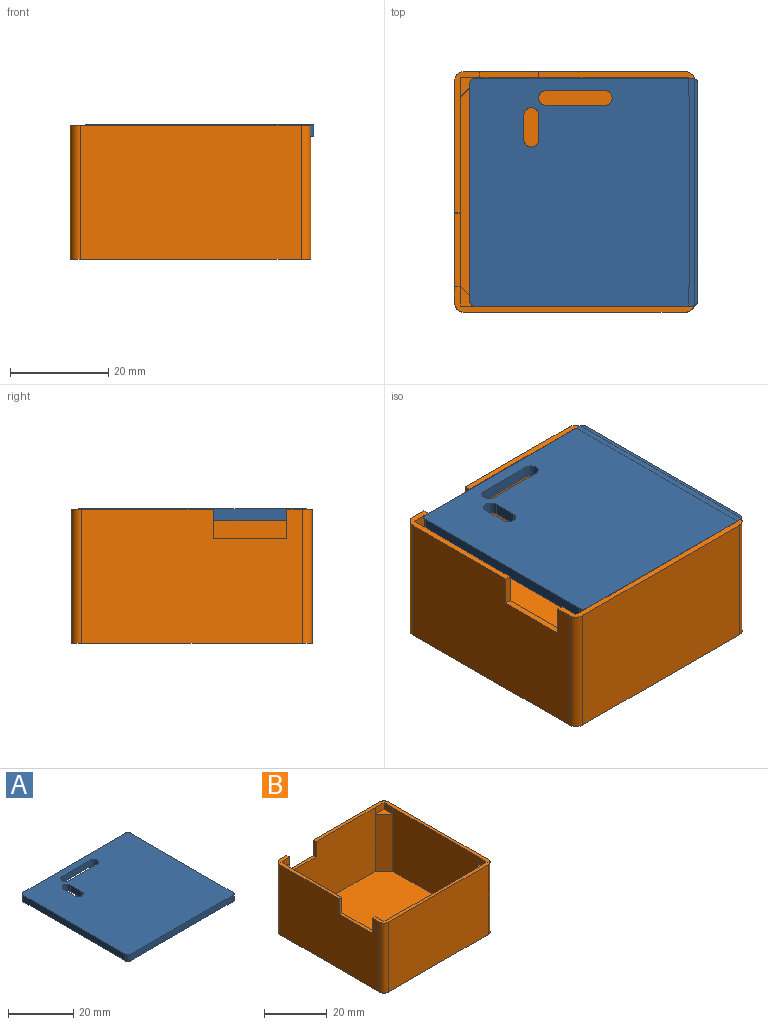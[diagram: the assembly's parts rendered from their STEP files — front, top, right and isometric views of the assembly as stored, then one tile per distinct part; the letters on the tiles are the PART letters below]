
ASSEMBLY  parts=2 mates=1
PART A: 18 faces, bbox 46.4x46.4x2.4 mm
  f0: plane 46.4x46.4mm, normal (0,0,1), area 2087mm2, adj f2,f3,f4,f5,f6,f7,f8,f9
  f1: plane 46.4x46.4mm, normal (0,0,-1), area 2087mm2, adj f2,f3,f4,f5,f6,f7,f8,f9
  f2: plane 44.4x2.4mm, normal (0,1,0), area 106.6mm2, adj f0,f1,f6,f9
  f3: plane 44.4x2.4mm, normal (-1,0,0), area 106.6mm2, adj f0,f1,f6,f7
  f4: plane 44.4x2.4mm, normal (0,-1,0), area 106.6mm2, adj f0,f1,f7,f8
  f5: plane 44.4x2.4mm, normal (1,0,0), area 106.6mm2, adj f0,f1,f8,f9
  f6: cylinder r=1mm len=2.4mm, axis (0,0,1), area 3.8mm2, adj f0,f1,f2,f3
  f7: cylinder r=1mm len=2.4mm, axis (0,0,-1), area 3.8mm2, adj f0,f1,f3,f4
  f8: cylinder r=1mm len=2.4mm, axis (0,0,1), area 3.8mm2, adj f0,f1,f4,f5
  f9: cylinder r=1mm len=2.4mm, axis (0,0,-1), area 3.8mm2, adj f0,f1,f2,f5
  f10: plane 12x2.4mm, normal (0,-1,0), area 28.8mm2, adj f0,f1,f16,f17
  f11: plane 12x2.4mm, normal (0,1,0), area 28.8mm2, adj f0,f1,f16,f17
  f12: plane 5x2.4mm, normal (1,0,0), area 12mm2, adj f0,f1,f14,f15
  f13: plane 5x2.4mm, normal (-1,0,0), area 12mm2, adj f0,f1,f14,f15
  f14: cylinder r=1.5mm len=3mm, axis (0,0,-1), area 11.3mm2, adj f0,f1,f12,f13
  f15: cylinder r=1.5mm len=3mm, axis (0,0,1), area 11.3mm2, adj f0,f1,f12,f13
  f16: cylinder r=1.5mm len=3mm, axis (0,0,-1), area 11.3mm2, adj f0,f1,f10,f11
  f17: cylinder r=1.5mm len=3mm, axis (0,0,-1), area 11.3mm2, adj f0,f1,f10,f11
PART B: 38 faces, bbox 49x49x27.3 mm
  f0: plane 28.8x5.2mm, normal (0,0,1), area 38.9mm2, adj f4,f5,f11,f14,f18,f29,f30,f32
  f1: plane 49x49mm, normal (0,0,1), area 156.3mm2, adj f2,f3,f4,f5,f6,f7,f9,f10
  f2: plane 24.9x4mm, normal (-0.71,-0.71,0), area 126.5mm2, adj f1,f9,f10,f13,f26,f27,f28
  f3: plane 24.9x4mm, normal (-0.71,0.71,0), area 126.5mm2, adj f1,f9,f12,f13,f20,f21,f22
  f4: plane 45x27.3mm, normal (0,1,0), area 1156.5mm2, adj f0,f1,f8,f14,f17,f35,f36,f37
  f5: plane 45x27.3mm, normal (-1,0,0), area 1138.5mm2, adj f0,f1,f8,f14,f15,f32,f33,f34
  f6: plane 45x27.3mm, normal (0,-1,0), area 1228.5mm2, adj f1,f8,f15,f16
  f7: plane 45x27.3mm, normal (1,0,0), area 1228.5mm2, adj f1,f8,f16,f17
  f8: plane 49x49mm, normal (0,0,-1), area 2397.6mm2, adj f4,f5,f6,f7,f14,f15,f16,f17
  f9: plane 38.6x24.9mm, normal (-1,0,0), area 961.1mm2, adj f1,f2,f3,f13
  f10: plane 38.6x24.9mm, normal (0,-1,0), area 889.1mm2, adj f1,f2,f13,f18,f35,f36
  f11: plane 38.6x24.9mm, normal (1,0,0), area 871.1mm2, adj f0,f13,f18,f19,f32,f33
  f12: plane 38.6x24.9mm, normal (0,1,0), area 961.1mm2, adj f1,f3,f13,f19
  f13: plane 46.6x46.6mm, normal (0,0,1), area 2139.6mm2, adj f2,f3,f9,f10,f11,f12,f18,f19
  f14: cylinder r=2mm len=27.3mm, axis (0,0,1), area 85.8mm2, adj f0,f4,f5,f8
  f15: cylinder r=2mm len=27.3mm, axis (0,0,-1), area 85.8mm2, adj f1,f5,f6,f8
  f16: cylinder r=2mm len=27.3mm, axis (0,0,1), area 85.8mm2, adj f1,f6,f7,f8
  f17: cylinder r=2mm len=27.3mm, axis (0,0,-1), area 85.8mm2, adj f1,f4,f7,f8
  f18: plane 24.9x4mm, normal (0.71,-0.71,0), area 126.5mm2, adj f0,f10,f11,f13,f29,f30,f31,f37
  f19: plane 24.9x4mm, normal (0.71,0.71,0), area 126.5mm2, adj f1,f11,f12,f13,f23,f24,f25,f34
  f20: plane 3.9x3.9mm, normal (0,0,1), area 7.6mm2, adj f3,f21,f22
  f21: plane 3.9x2.6mm, normal (0,1,0), area 10.1mm2, adj f1,f3,f20,f22
  f22: plane 3.9x2.6mm, normal (-1,0,0), area 10.1mm2, adj f1,f3,f20,f21
  f23: plane 3.9x3.9mm, normal (0,0,1), area 7.6mm2, adj f19,f24,f25
  f24: plane 3.9x2.6mm, normal (0,1,0), area 10.1mm2, adj f1,f19,f23,f25
  f25: plane 3.9x2.6mm, normal (1,0,0), area 10.1mm2, adj f1,f19,f23,f24
  f26: plane 3.9x3.9mm, normal (0,0,1), area 7.6mm2, adj f2,f27,f28
  f27: plane 3.9x2.6mm, normal (0,-1,0), area 10.1mm2, adj f1,f2,f26,f28
  f28: plane 3.9x2.6mm, normal (-1,0,0), area 10.1mm2, adj f1,f2,f26,f27
  f29: plane 3.9x2.6mm, normal (0,-1,0), area 10.1mm2, adj f0,f18,f30,f31
  f30: plane 3.9x2.6mm, normal (1,0,0), area 10.1mm2, adj f0,f18,f29,f31
  f31: plane 3.9x3.9mm, normal (0,0,1), area 7.6mm2, adj f18,f29,f30
  f32: plane 6x1.2mm, normal (0,-1,0), area 7.2mm2, adj f0,f5,f11,f33
  f33: plane 15x1.2mm, normal (0,0,1), area 18mm2, adj f5,f11,f32,f34
  f34: plane 6x1.2mm, normal (0,1,0), area 7.2mm2, adj f1,f5,f19,f33
  f35: plane 6x1.2mm, normal (-1,0,0), area 7.2mm2, adj f1,f4,f10,f36
  f36: plane 12x1.2mm, normal (0,0,1), area 14.4mm2, adj f4,f10,f35,f37
  f37: plane 6x1.2mm, normal (1,0,0), area 7.2mm2, adj f0,f4,f18,f36
PLACE A t=(-73.68,-3.22,25)mm
PLACE B at identity fixed
MATE slider B.f13 <-> A.f0  axis (0,0,1) through (-41.84,40.26,2.4)mm
